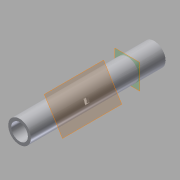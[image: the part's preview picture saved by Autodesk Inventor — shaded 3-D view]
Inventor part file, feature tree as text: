
AUTODESK INVENTOR PART (.ipt)
format: ipt  version: 2013 (Build 170138000, 138)  size: 100,352 bytes
history: native  units: in
note: dims shown in document units (in); Inventor stores cm internally (conversion verified against a paired STEP export)
features: extrude x3, sketch x3, plane x2
ambient origin geometry x8: Origin, YZ Plane, XZ Plane, XY Plane, X Axis, Y Axis, Z Axis, Center Point
bodies: Solid1 (feature_tree)
feature tree (8):
  extrude  "Extrusion1"  Depth=0.84in
  plane  "Work Plane1"
  extrude  "Extrusion3"  [1 undecoded]
  plane  "Work Plane3"
  extrude  "Extrusion4"  Depth=0.25in TaperAngle=0.0deg
  sketch  "Sketch1"  dims[d0=0.622in d2=0.84in]
  sketch  "Sketch3"  dims[d3=5.0in d4=0.0in d7=-1.0in]
  sketch  "Sketch4"  dims[d8=0.125in d9=0.0in d10=0.25in d11=0.0in]
note: 1 required parameter value undecoded (feature->parameter linkage not recoverable at this tier; creation-order binding heuristic only, values carry confidence <= 0.55)
